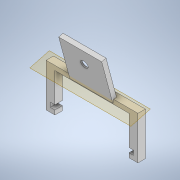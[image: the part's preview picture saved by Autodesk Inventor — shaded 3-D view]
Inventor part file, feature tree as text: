
AUTODESK INVENTOR PART (.ipt)
format: ipt  version: 2020.2 (Build 242310000, 310)  size: 161,280 bytes
history: native  units: mm
features: extrude x4, sketch x4, other x1
ambient origin geometry x8: Origin, YZ Plane, XZ Plane, XY Plane, X Axis, Y Axis, Z Axis, Center Point
bodies: Solide1 (feature_tree)
feature tree (9):
  extrude  "Extrusion1"  Depth=56.0mm
  other  "Plan de construction1"
  extrude  "Extrusion2"  Depth=3.0mm
  extrude  "Extrusion3"  Depth=3.0mm
  extrude  "Extrusion4"  Depth=3.0mm
  sketch  "Esquisse1"
  sketch  "Esquisse2"
  sketch  "Esquisse3"
  sketch  "Esquisse4"
